# Revit family: GP_ФБС_R15
name_source: partatom
category: Обобщенные модели
revit_build: Autodesk Revit 2015 (Build: 20140322_1515(x64)
units: mm (PartAtom-declared; Revit-internal decimal feet)

## types (15) — shared parameters
ADSK_URL страницы изделия = http://gbi-podolsk.ru
GP_Адрес = Московская область, г. Подольск, ул. Шамотная, д. 11А
GP_Водонепроницаемость = W2
GP_Контактный телефон = ‎8-495-999-46-60, ‎8-916-155-11-85
GP_Логотип компании = Логотип.jpg
GP_Морозостойкость = F100
GP_Прочность = B7.5
d2 = 40 мм
d3 = 40 мм
l2 = 100 мм
Изготовитель = ООО «Компания Фурор-Строй»
Изображение типоразмера = ФБС.png
Материал несущих конструкций = Бетон_B7.5_F100_W2
Описание = Фундаментный бетонный блок

## per-type parameters (varying)
| type | ADSK_Марка | ADSK_Наименование | ADSK_Размер_Высота | ADSK_Размер_Длина | ADSK_Размер_Ширина | GP_Масса | GP_Объем | d1 | l1 | Группа модели | Стоимость |
| ФБС24.3.6-Т | 24.3.6-Т | Фундаментный бетонный блок 24.3.6-Т | 580 мм | 2380 мм | 300 мм | 0.970 t | 0.41 м³ | 50 мм | 20 мм | ФБС | 1700 $ |
| ФБС9.3.6-Т | 9.3.6-Т | Фундаментный бетонный блок 9.3.6-Т | 580 мм | 880 мм | 300 мм | 0.350 t | 0.15 м³ | 50 мм | 20 мм | ФБС | 820 $ |
| ФБС24.4.6-Т | 24.4.6-Т | Фундаментный бетонный блок 24.4.6-Т | 580 мм | 2380 мм | 400 мм | 1.300 t | 0.54 м³ | 80 мм | 30 мм | ФБС | 2100 $ |
| ФБС12.4.6-Т | 12.4.6-Т | Фундаментный бетонный блок 12.4.6-Т | 580 мм | 1180 мм | 400 мм | 0.640 t | 0.27 м³ | 80 мм | 30 мм | ФБС | 1250 $ |
| ФБС12.4.3-Т | 12.4.3-Т | Фундаментный бетонный блок 12.4.3-Т | 280 мм | 1180 мм | 400 мм | 0.310 t | 0.13 м³ | 80 мм | 30 мм |  | 750 $ |
| ФБС9.4.6-Т | 9.4.6-Т | Фундаментный бетонный блок 9.4.6-Т | 580 мм | 880 мм | 400 мм | 0.470 t | 0.20 м³ | 80 мм | 30 мм | ФБС | 1030 $ |
| ФБС24.5.6-Т | 24.5.6-Т | Фундаментный бетонный блок 24.5.6-Т | 580 мм | 2380 мм | 500 мм | 1.630 t | 0.68 м³ | 100 мм | 30 мм | ФБС | 2550 $ |
| ФБС12.5.6-Т | 12.5.6-Т | Фундаментный бетонный блок 12.5.6-Т | 580 мм | 1180 мм | 500 мм | 0.790 t | 0.33 м³ | 100 мм | 30 мм | ФБС | 1425 $ |
| ФБС12.5.3-Т | 12.5.3-Т | Фундаментный бетонный блок 12.5.3-Т | 280 мм | 1180 мм | 500 мм | 0.380 t | 0.16 м³ | 100 мм | 30 мм | ФБС | 950 $ |
| ФБС9.5.6-Т | 9.5.6-Т | Фундаментный бетонный блок 9.5.6-Т | 580 мм | 880 мм | 500 мм | 0.590 t | 0.24 м³ | 100 мм | 30 мм | ФБС | 1250 $ |
| ФБС24.6.6-Т | 24.6.6-Т | Фундаментный бетонный блок 24.6.6-Т | 580 мм | 2380 мм | 600 мм | 1.960 t | 0.82 м³ | 120 мм | 30 мм | ФБС | 3200 $ |
| ФБС12.6.6-Т | 12.6.6-Т | Фундаментный бетонный блок 12.6.6-Т | 580 мм | 1180 мм | 600 мм | 0.960 t | 0.40 м³ | 120 мм | 30 мм | ФБС | 1850 $ |
| ФБС12.6.3-Т | 12.6.3-Т | Фундаментный бетонный блок 12.6.3-Т | 280 мм | 1180 мм | 600 мм | 0.460 t | 0.19 м³ | 120 мм | 30 мм | ФБС | 1150 $ |
| ФБС9.6.6-Т | 9.6.6-Т | Фундаментный бетонный блок 9.6.6-Т | 580 мм | 880 мм | 600 мм | 0.700 t | 0.29 м³ | 120 мм | 30 мм |  | 1500 $ |
| ФБС12.3.6-Т ТУ | 12.3.6-Т ТУ | Фундаментный бетонный блок 12.3.6-Т ТУ | 580 мм | 1180 мм | 400 мм | 0.310 t | 0.13 м³ | 80 мм | 30 мм |  | 750 $ |
